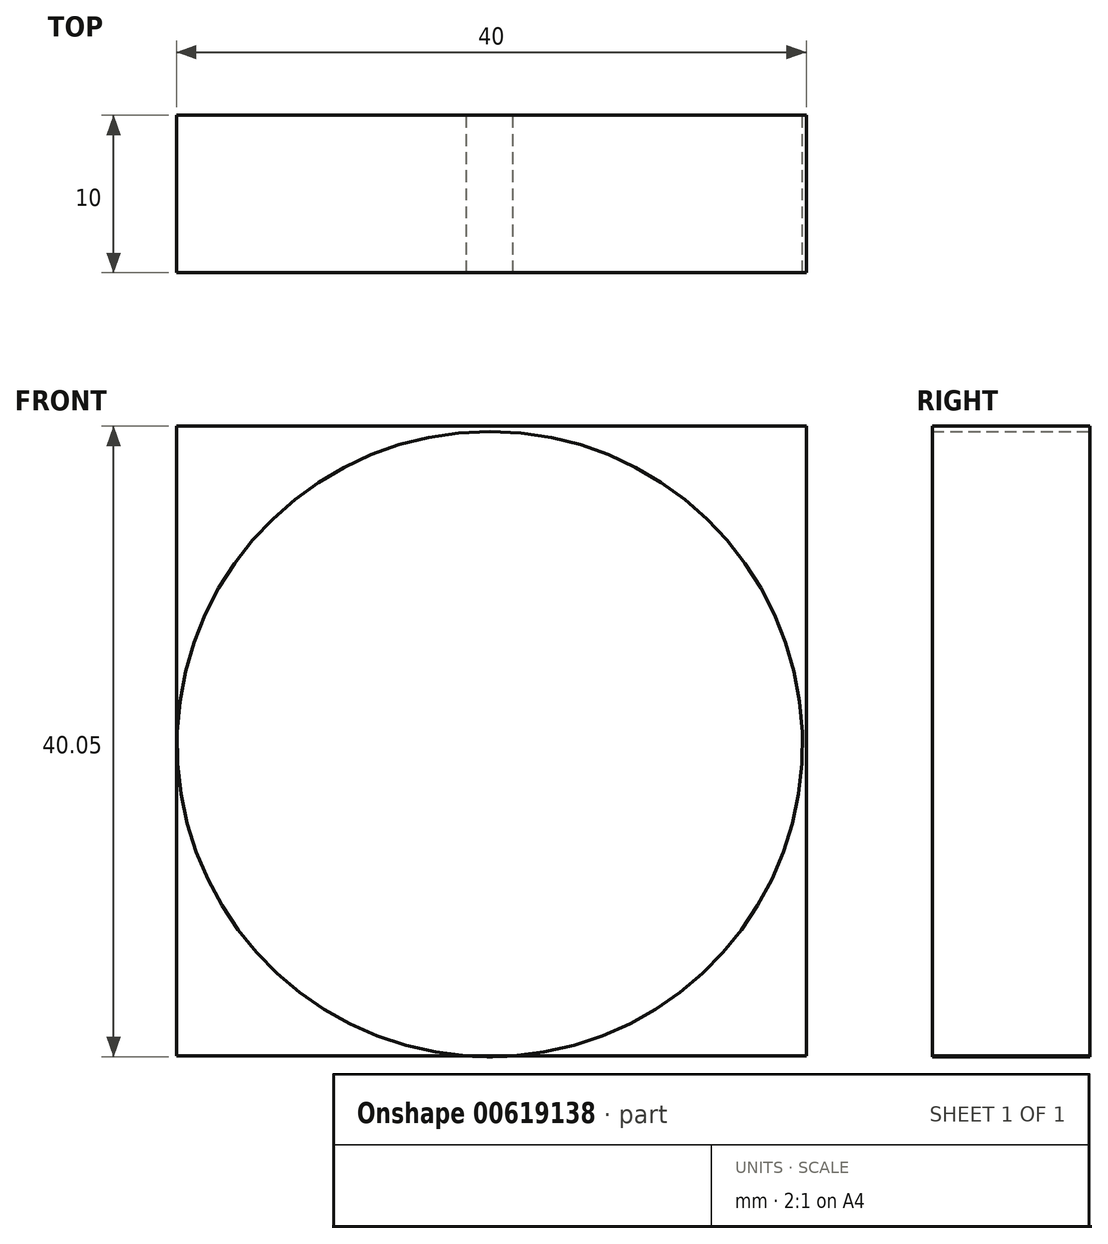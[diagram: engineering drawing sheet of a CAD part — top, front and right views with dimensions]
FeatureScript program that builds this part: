
annotation { "Feature Type Name" : "Feature", "Feature Type Description" : "" }
export const myFeature = defineFeature(function(context is Context, id is Id, definition is map)
    precondition{}
    {
        {
            var Q0;
            Q0=qCreatedBy(makeId("Front.planeOp"),FACE);
            var sketch = newSketch(context, id + "F0", { "sketchPlane" : qUnion([Q0])});
            skLineSegment(sketch, "E0.bottom", {"start": v(-37.84, 26.3) * mm, "end": v(2.16, 26.3) * mm});
            skLineSegment(sketch, "E0.top", {"start": v(-37.84, -13.7) * mm, "end": v(2.16, -13.7) * mm});
            skLineSegment(sketch, "E0.left", {"start": v(-37.84, 26.3) * mm, "end": v(-37.84, -13.7) * mm});
            skLineSegment(sketch, "E0.right", {"start": v(2.16, 26.3) * mm, "end": v(2.16, -13.7) * mm});
            skCircle(sketch, "E1", {"center": v(-17.94, 6.1) * mm, "radius": 19.86 * mm});
            skSolve(sketch);
        }
        {
            var Q0;
            Q0=makeQuery(id+"F0.imprint","IMPRINT",FACE,{"disambiguationData":[TD([[makeQuery(id+"F0.imprint","IMPRINT",EDGE,{"derivedFrom":sQuery(id+"F0.wireOp",EDGE,"E0.bottom")}),-1.0]])]});
            var Q1;
            {var subQ0=sQuery(id+"F0.wireOp",EDGE,"E1");var subQ1=sQuery(id+"F0.wireOp",EDGE,"E0.top");var subQ2=makeQuery(id+"F0.imprint","INTERSECT",VERTEX,{"disambiguationData":[OD(0.0)],"derivedFrom":[subQ1,subQ0]});Q1=makeQuery(id+"F0.imprint","IMPRINT",FACE,{"disambiguationData":[TD([[makeQuery(id+"F0.imprint","IMPRINT",EDGE,{"disambiguationData":[TD([[subQ2,-1.0]])],"derivedFrom":subQ1}),-1.0]])]});}
            extrude(context, id + "F1", {"entities" : qUnion([Q0, Q1]), "depth" : 10 * mm, "offsetDistance" : 25 * mm});
        }
    });
